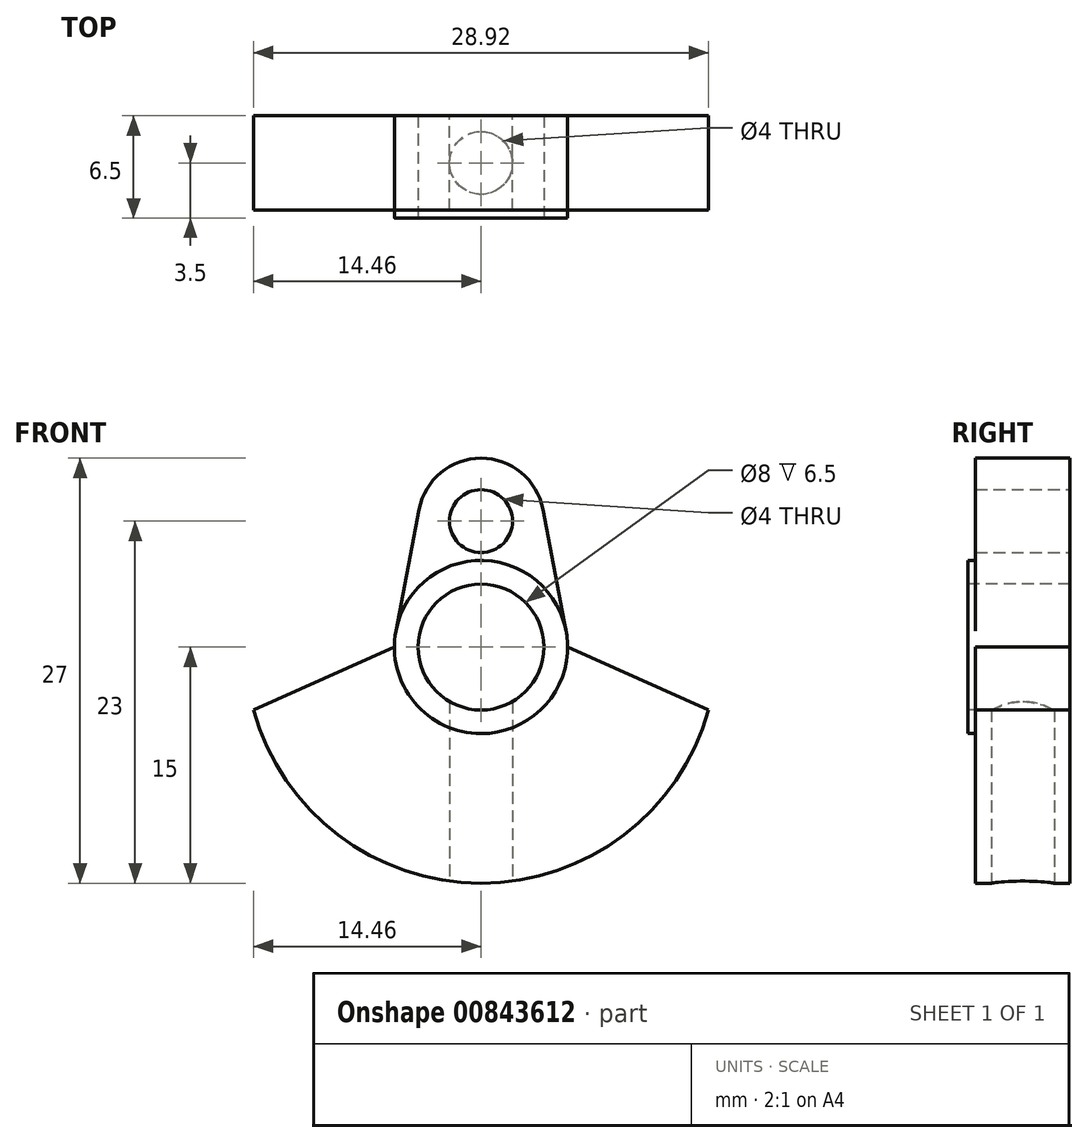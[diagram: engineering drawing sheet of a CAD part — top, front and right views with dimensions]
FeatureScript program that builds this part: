
annotation { "Feature Type Name" : "Feature", "Feature Type Description" : "" }
export const myFeature = defineFeature(function(context is Context, id is Id, definition is map)
    precondition{}
    {
        {
            var Q0;
            Q0=qCreatedBy(makeId("Front.planeOp"),FACE);
            var sketch = newSketch(context, id + "F0", { "sketchPlane" : qUnion([Q0])});
            skCircle(sketch, "E0", {"center": v(0, 8) * mm, "radius": 2 * mm});
            skCircle(sketch, "E1", {"center": v(0, 0) * mm, "radius": 5.5 * mm, "construction": true});
            skArc(sketch, "E2", {"start": v(-14.46, -4) * mm, "mid": v(0, -15) * mm, "end": v(14.46, -4) * mm});
            skLineSegment(sketch, "E3", {"start": v(-14.46, -4) * mm, "end": v(-5.5, 0) * mm});
            skLineSegment(sketch, "E4", {"start": v(14.46, -4) * mm, "end": v(5.5, 0) * mm});
            skArc(sketch, "E5", {"start": v(3.93, 8.75) * mm, "mid": v(0, 12) * mm, "end": v(-3.93, 8.75) * mm});
            skLineSegment(sketch, "E6", {"start": v(5.4, 1.03) * mm, "end": v(3.93, 8.75) * mm});
            skLineSegment(sketch, "E7", {"start": v(-3.93, 8.75) * mm, "end": v(-5.4, 1.03) * mm});
            skArc(sketch, "E8", {"start": v(-5.4, 1.03) * mm, "mid": v(-5.48, 0.52) * mm, "end": v(-5.5, 0) * mm});
            skArc(sketch, "E9", {"start": v(5.4, 1.03) * mm, "mid": v(5.48, 0.52) * mm, "end": v(5.5, 0) * mm});
            skSolve(sketch);
        }
        {
            var Q0;
            Q0=makeQuery(id+"F0.imprint","IMPRINT",FACE,{"disambiguationData":[TD([[makeQuery(id+"F0.imprint","IMPRINT",EDGE,{"derivedFrom":sQuery(id+"F0.wireOp",EDGE,"E0")}),-1.0]])]});
            extrude(context, id + "F1", {"entities" : qUnion([Q0]), "depth" : 6 * mm, "offsetDistance" : 25 * mm});
        }
        {
            var Q0;
            Q0=makeQuery(id+"F1.opExtrude","CAP_FACE",FACE,{"disambiguationData":[OSD([sQuery(id+"F0.wireOp",EDGE,"E0"),sQuery(id+"F0.wireOp",EDGE,"E2"),sQuery(id+"F0.wireOp",EDGE,"E3"),sQuery(id+"F0.wireOp",EDGE,"E4"),sQuery(id+"F0.wireOp",EDGE,"E5"),sQuery(id+"F0.wireOp",EDGE,"E6"),sQuery(id+"F0.wireOp",EDGE,"E7"),sQuery(id+"F0.wireOp",EDGE,"E8"),sQuery(id+"F0.wireOp",EDGE,"E9")])],"isStart":false});
            var sketch = newSketch(context, id + "F2", { "sketchPlane" : qUnion([Q0])});
            skArc(sketch, "E10.0", {"start": v(5.4, 1.03) * mm, "mid": v(5.48, 0.52) * mm, "end": v(5.5, 0) * mm});
            skCircle(sketch, "E11", {"center": v(0, 0) * mm, "radius": 4 * mm});
            skSolve(sketch);
        }
        {
            var Q0;
            Q0=makeQuery(id+"F2.imprint","IMPRINT",FACE,{"disambiguationData":[TD([[makeQuery(id+"F2.imprint","IMPRINT",EDGE,{"derivedFrom":sQuery(id+"F2.wireOp",EDGE,"E11")}),1.0]])]});
            extrude(context, id + "F3", {"entities" : qUnion([Q0]), "operationType" : NewBodyOperationType.REMOVE, "oppositeDirection" : true, "depth" : 25 * mm, "offsetDistance" : 25 * mm});
        }
        {
            var Q0;
            Q0=makeQuery(id+"F1.opExtrude","CAP_FACE",FACE,{"disambiguationData":[OSD([sQuery(id+"F0.wireOp",EDGE,"E0"),sQuery(id+"F0.wireOp",EDGE,"E2"),sQuery(id+"F0.wireOp",EDGE,"E3"),sQuery(id+"F0.wireOp",EDGE,"E4"),sQuery(id+"F0.wireOp",EDGE,"E5"),sQuery(id+"F0.wireOp",EDGE,"E6"),sQuery(id+"F0.wireOp",EDGE,"E7"),sQuery(id+"F0.wireOp",EDGE,"E8"),sQuery(id+"F0.wireOp",EDGE,"E9")])],"isStart":false});
            var sketch = newSketch(context, id + "F4", { "sketchPlane" : qUnion([Q0])});
            skCircle(sketch, "E12.0", {"center": v(0, 0) * mm, "radius": 4 * mm});
            skCircle(sketch, "E13", {"center": v(0, 0) * mm, "radius": 5.5 * mm});
            skSolve(sketch);
        }
        {
            var Q0;
            Q0=makeQuery(id+"F4.imprint","IMPRINT",FACE,{"disambiguationData":[TD([[makeQuery(id+"F4.imprint","IMPRINT",EDGE,{"derivedFrom":sQuery(id+"F4.wireOp",EDGE,"E12.0")}),-1.0]])]});
            extrude(context, id + "F5", {"entities" : qUnion([Q0]), "operationType" : NewBodyOperationType.ADD, "depth" : .5 * mm, "offsetDistance" : 25 * mm});
        }
        {
            var Q0;
            Q0=qCreatedBy(makeId("Top.planeOp"),FACE);
            cPlane(context, id + "F6", {"entities" : qUnion([Q0]), "cplaneType" : CPlaneType.OFFSET, "offset" : 15 * mm, "oppositeDirection" : true, "width" : 150 * mm, "height" : 150 * mm});
        }
        {
            var Q0;
            Q0=qCreatedBy(id+"F6.planeOp",FACE);
            var sketch = newSketch(context, id + "F7", { "sketchPlane" : qUnion([Q0])});
            skCircle(sketch, "E14", {"center": v(0, -3) * mm, "radius": 2 * mm});
            skSolve(sketch);
        }
        {
            var Q0;
            Q0 = qSketchRegion(id + "F7", true);
            var Q1;
            Q1=makeQuery(id+"F5.boolean.opBoolean","MERGE",FACE,{"derivedFrom":[makeQuery(id+"F3.boolean.opBoolean","COPY",FACE,{"derivedFrom":makeQuery(id+"F3.opExtrude","SWEPT_FACE",FACE,{"disambiguationData":[OSD([sQuery(id+"F2.wireOp",EDGE,"E11")])]})}),makeQuery(id+"F5.opExtrude","SWEPT_FACE",FACE,{"disambiguationData":[OSD([sQuery(id+"F4.wireOp",EDGE,"E12.0")])]})]});
            extrude(context, id + "F8", {"entities" : qUnion([Q0]), "operationType" : NewBodyOperationType.REMOVE, "endBound" : BoundingType.UP_TO_SURFACE, "depth" : 25 * mm, "endBoundEntityFace" : qUnion([Q1]), "offsetDistance" : 25 * mm});
        }
    });
